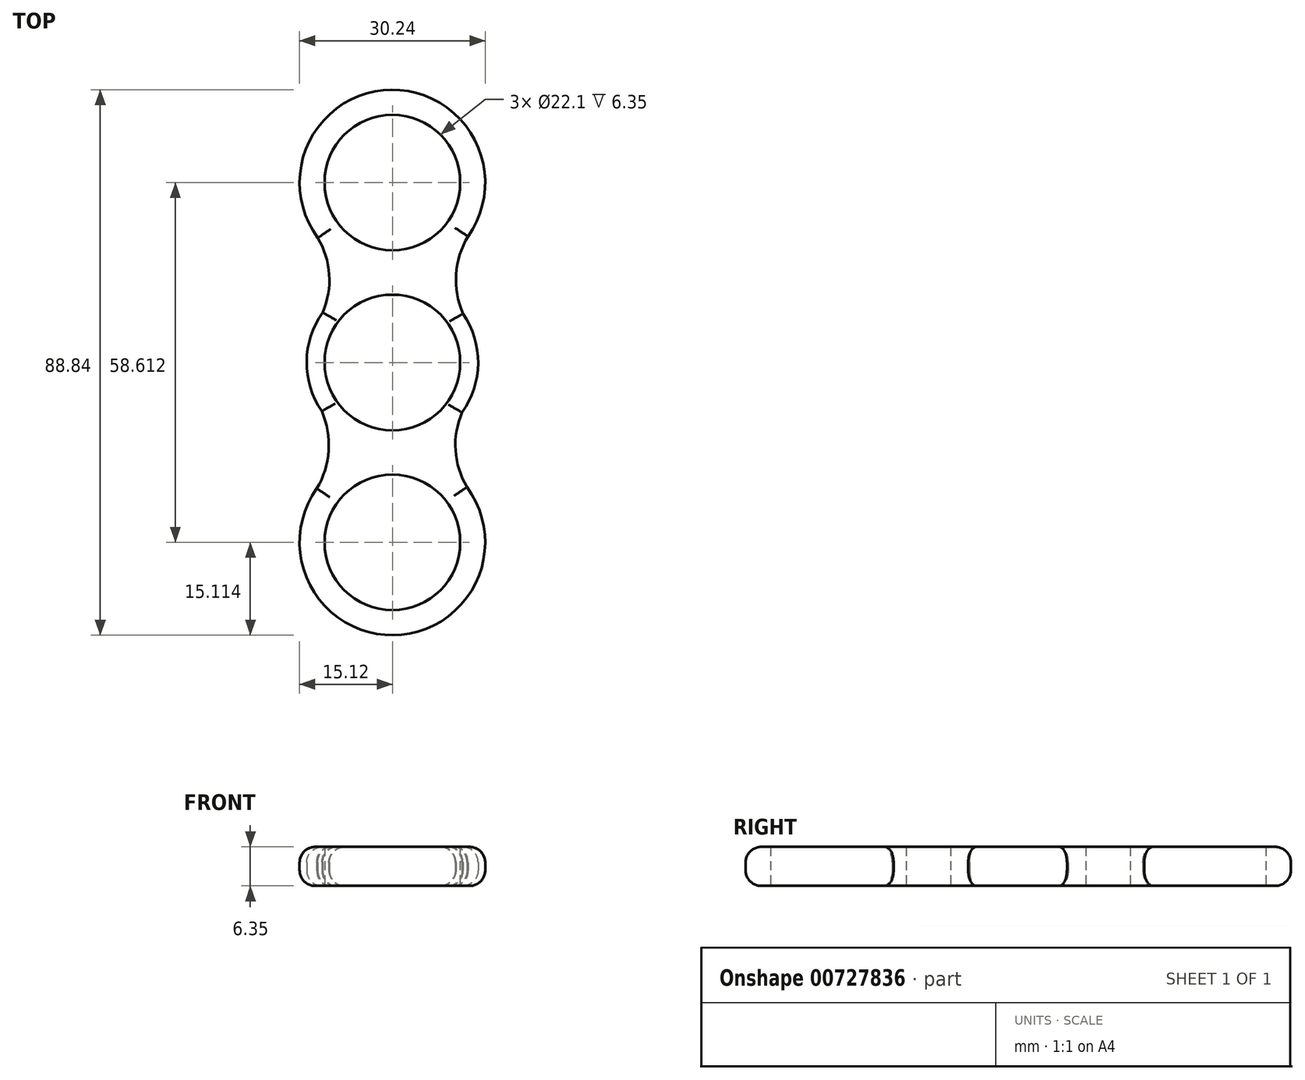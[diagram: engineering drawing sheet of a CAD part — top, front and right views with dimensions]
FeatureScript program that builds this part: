
annotation { "Feature Type Name" : "Feature", "Feature Type Description" : "" }
export const myFeature = defineFeature(function(context is Context, id is Id, definition is map)
    precondition{}
    {
        {
            var Q0;
            Q0=qCreatedBy(makeId("Top.planeOp"),FACE);
            var sketch = newSketch(context, id + "F0", { "sketchPlane" : qUnion([Q0])});
            skCircle(sketch, "E0", {"center": v(0, 0) * mm, "radius": 11.05 * mm});
            skCircle(sketch, "E1", {"center": v(0, 0) * mm, "radius": 13.97 * mm});
            skCircle(sketch, "E2", {"center": v(0, 29.3) * mm, "radius": 11.05 * mm});
            skCircle(sketch, "E3", {"center": v(0, 29.3) * mm, "radius": 15.12 * mm});
            skCircle(sketch, "E4.1.0", {"center": v(0, -29.3) * mm, "radius": 11.05 * mm});
            skCircle(sketch, "E4.1.1", {"center": v(0, -29.3) * mm, "radius": 15.12 * mm});
            skArc(sketch, "E5", {"start": v(12.96, 21.52) * mm, "mid": v(10.36, 13.55) * mm, "end": v(12.83, 5.54) * mm});
            skArc(sketch, "E6", {"start": v(-12.83, 5.54) * mm, "mid": v(-10.27, 13.55) * mm, "end": v(-12.96, 21.52) * mm});
            skArc(sketch, "E7.1.0", {"start": v(-12.96, -21.52) * mm, "mid": v(-10.36, -13.55) * mm, "end": v(-12.83, -5.54) * mm});
            skArc(sketch, "E7.1.1", {"start": v(12.83, -5.54) * mm, "mid": v(10.27, -13.55) * mm, "end": v(12.96, -21.52) * mm});
            skSolve(sketch);
        }
        {
            var Q0;
            Q0 = qSketchRegion(id + "F0", true);
            extrude(context, id + "F1", {"entities" : qUnion([Q0]), "depth" : 6.35 * mm, "offsetDistance" : 25.4 * mm});
        }
        {
            var Q0;
            Q0=makeQuery(id+"F1.opExtrude","CAP_EDGE",EDGE,{"disambiguationData":[OSD([sQuery(id+"F0.wireOp",EDGE,"E3")])],"isStart":false});
            var Q1;
            {var subQ0=sQuery(id+"F0.wireOp",EDGE,"E7.1.0");var subQ1=sQuery(id+"F0.wireOp",EDGE,"E1");var subQ2=makeQuery(id+"F0.imprint","INTERSECT",VERTEX,{"disambiguationData":[OD(0.0)],"derivedFrom":[subQ1,subQ0]});var subQ3=sQuery(id+"F0.wireOp",EDGE,"E6");var subQ4=makeQuery(id+"F0.imprint","INTERSECT",VERTEX,{"disambiguationData":[OD(0.0)],"derivedFrom":[subQ1,subQ3]});Q1=makeQuery(id+"F1.opExtrude","CAP_EDGE",EDGE,{"disambiguationData":[OSD([subQ1]),TDD([makeQuery(id+"F0.imprint","IMPRINT",EDGE,{"disambiguationData":[TD([[subQ4,1.0]])],"derivedFrom":subQ1}),makeQuery(id+"F0.imprint","IMPRINT",EDGE,{"disambiguationData":[TD([[subQ4,-1.0]])],"derivedFrom":subQ1}),makeQuery(id+"F0.imprint","IMPRINT",EDGE,{"disambiguationData":[TD([[subQ2,-1.0]])],"derivedFrom":subQ1})])],"isStart":false});}
            var Q2;
            Q2=makeQuery(id+"F1.opExtrude","CAP_EDGE",EDGE,{"disambiguationData":[OSD([sQuery(id+"F0.wireOp",EDGE,"E6")])],"isStart":false});
            var Q3;
            Q3=makeQuery(id+"F1.opExtrude","CAP_EDGE",EDGE,{"disambiguationData":[OSD([sQuery(id+"F0.wireOp",EDGE,"E7.1.0")])],"isStart":false});
            var Q4;
            Q4=makeQuery(id+"F1.opExtrude","CAP_EDGE",EDGE,{"disambiguationData":[OSD([sQuery(id+"F0.wireOp",EDGE,"E4.1.1")])],"isStart":false});
            var Q5;
            Q5=makeQuery(id+"F1.opExtrude","CAP_EDGE",EDGE,{"disambiguationData":[OSD([sQuery(id+"F0.wireOp",EDGE,"E7.1.1")])],"isStart":false});
            var Q6;
            {var subQ0=sQuery(id+"F0.wireOp",EDGE,"E5");var subQ1=sQuery(id+"F0.wireOp",EDGE,"E1");var subQ2=makeQuery(id+"F0.imprint","INTERSECT",VERTEX,{"disambiguationData":[OD(0.0)],"derivedFrom":[subQ1,subQ0]});var subQ3=sQuery(id+"F0.wireOp",EDGE,"E7.1.1");var subQ4=makeQuery(id+"F0.imprint","INTERSECT",VERTEX,{"disambiguationData":[OD(0.0)],"derivedFrom":[subQ1,subQ3]});Q6=makeQuery(id+"F1.opExtrude","CAP_EDGE",EDGE,{"disambiguationData":[OSD([subQ1]),TDD([makeQuery(id+"F0.imprint","IMPRINT",EDGE,{"disambiguationData":[TD([[subQ2,-1.0]])],"derivedFrom":subQ1}),makeQuery(id+"F0.imprint","IMPRINT",EDGE,{"disambiguationData":[TD([[subQ4,1.0]])],"derivedFrom":subQ1}),makeQuery(id+"F0.imprint","IMPRINT",EDGE,{"disambiguationData":[TD([[subQ2,1.0]])],"derivedFrom":subQ1})])],"isStart":false});}
            var Q7;
            Q7=makeQuery(id+"F1.opExtrude","CAP_EDGE",EDGE,{"disambiguationData":[OSD([sQuery(id+"F0.wireOp",EDGE,"E5")])],"isStart":false});
            fillet(context, id + "F2", {"entities" : qUnion([Q0, Q1, Q2, Q3, Q4, Q5, Q6, Q7]), "radius" : 2.54 * mm, "tangentPropagation" : true, "allowEdgeOverflow" : false});
        }
        {
            var Q0;
            Q0=makeQuery(id+"F1.opExtrude","CAP_EDGE",EDGE,{"disambiguationData":[OSD([sQuery(id+"F0.wireOp",EDGE,"E4.1.1")])],"isStart":true});
            var Q1;
            Q1=makeQuery(id+"F1.opExtrude","CAP_EDGE",EDGE,{"disambiguationData":[OSD([sQuery(id+"F0.wireOp",EDGE,"E7.1.0")])],"isStart":true});
            var Q2;
            {var subQ0=sQuery(id+"F0.wireOp",EDGE,"E7.1.0");var subQ1=sQuery(id+"F0.wireOp",EDGE,"E1");var subQ2=makeQuery(id+"F0.imprint","INTERSECT",VERTEX,{"disambiguationData":[OD(0.0)],"derivedFrom":[subQ1,subQ0]});var subQ3=sQuery(id+"F0.wireOp",EDGE,"E6");var subQ4=makeQuery(id+"F0.imprint","INTERSECT",VERTEX,{"disambiguationData":[OD(0.0)],"derivedFrom":[subQ1,subQ3]});Q2=makeQuery(id+"F1.opExtrude","CAP_EDGE",EDGE,{"disambiguationData":[OSD([subQ1]),TDD([makeQuery(id+"F0.imprint","IMPRINT",EDGE,{"disambiguationData":[TD([[subQ4,1.0]])],"derivedFrom":subQ1}),makeQuery(id+"F0.imprint","IMPRINT",EDGE,{"disambiguationData":[TD([[subQ4,-1.0]])],"derivedFrom":subQ1}),makeQuery(id+"F0.imprint","IMPRINT",EDGE,{"disambiguationData":[TD([[subQ2,-1.0]])],"derivedFrom":subQ1})])],"isStart":true});}
            var Q3;
            Q3=makeQuery(id+"F1.opExtrude","CAP_EDGE",EDGE,{"disambiguationData":[OSD([sQuery(id+"F0.wireOp",EDGE,"E6")])],"isStart":true});
            var Q4;
            Q4=makeQuery(id+"F1.opExtrude","CAP_EDGE",EDGE,{"disambiguationData":[OSD([sQuery(id+"F0.wireOp",EDGE,"E3")])],"isStart":true});
            var Q5;
            Q5=makeQuery(id+"F1.opExtrude","CAP_EDGE",EDGE,{"disambiguationData":[OSD([sQuery(id+"F0.wireOp",EDGE,"E5")])],"isStart":true});
            var Q6;
            {var subQ0=sQuery(id+"F0.wireOp",EDGE,"E5");var subQ1=sQuery(id+"F0.wireOp",EDGE,"E1");var subQ2=makeQuery(id+"F0.imprint","INTERSECT",VERTEX,{"disambiguationData":[OD(0.0)],"derivedFrom":[subQ1,subQ0]});var subQ3=sQuery(id+"F0.wireOp",EDGE,"E7.1.1");var subQ4=makeQuery(id+"F0.imprint","INTERSECT",VERTEX,{"disambiguationData":[OD(0.0)],"derivedFrom":[subQ1,subQ3]});Q6=makeQuery(id+"F1.opExtrude","CAP_EDGE",EDGE,{"disambiguationData":[OSD([subQ1]),TDD([makeQuery(id+"F0.imprint","IMPRINT",EDGE,{"disambiguationData":[TD([[subQ2,-1.0]])],"derivedFrom":subQ1}),makeQuery(id+"F0.imprint","IMPRINT",EDGE,{"disambiguationData":[TD([[subQ4,1.0]])],"derivedFrom":subQ1}),makeQuery(id+"F0.imprint","IMPRINT",EDGE,{"disambiguationData":[TD([[subQ2,1.0]])],"derivedFrom":subQ1})])],"isStart":true});}
            var Q7;
            Q7=makeQuery(id+"F1.opExtrude","CAP_EDGE",EDGE,{"disambiguationData":[OSD([sQuery(id+"F0.wireOp",EDGE,"E7.1.1")])],"isStart":true});
            fillet(context, id + "F3", {"entities" : qUnion([Q0, Q1, Q2, Q3, Q4, Q5, Q6, Q7]), "radius" : 2.54 * mm, "tangentPropagation" : true, "allowEdgeOverflow" : false});
        }
    });
